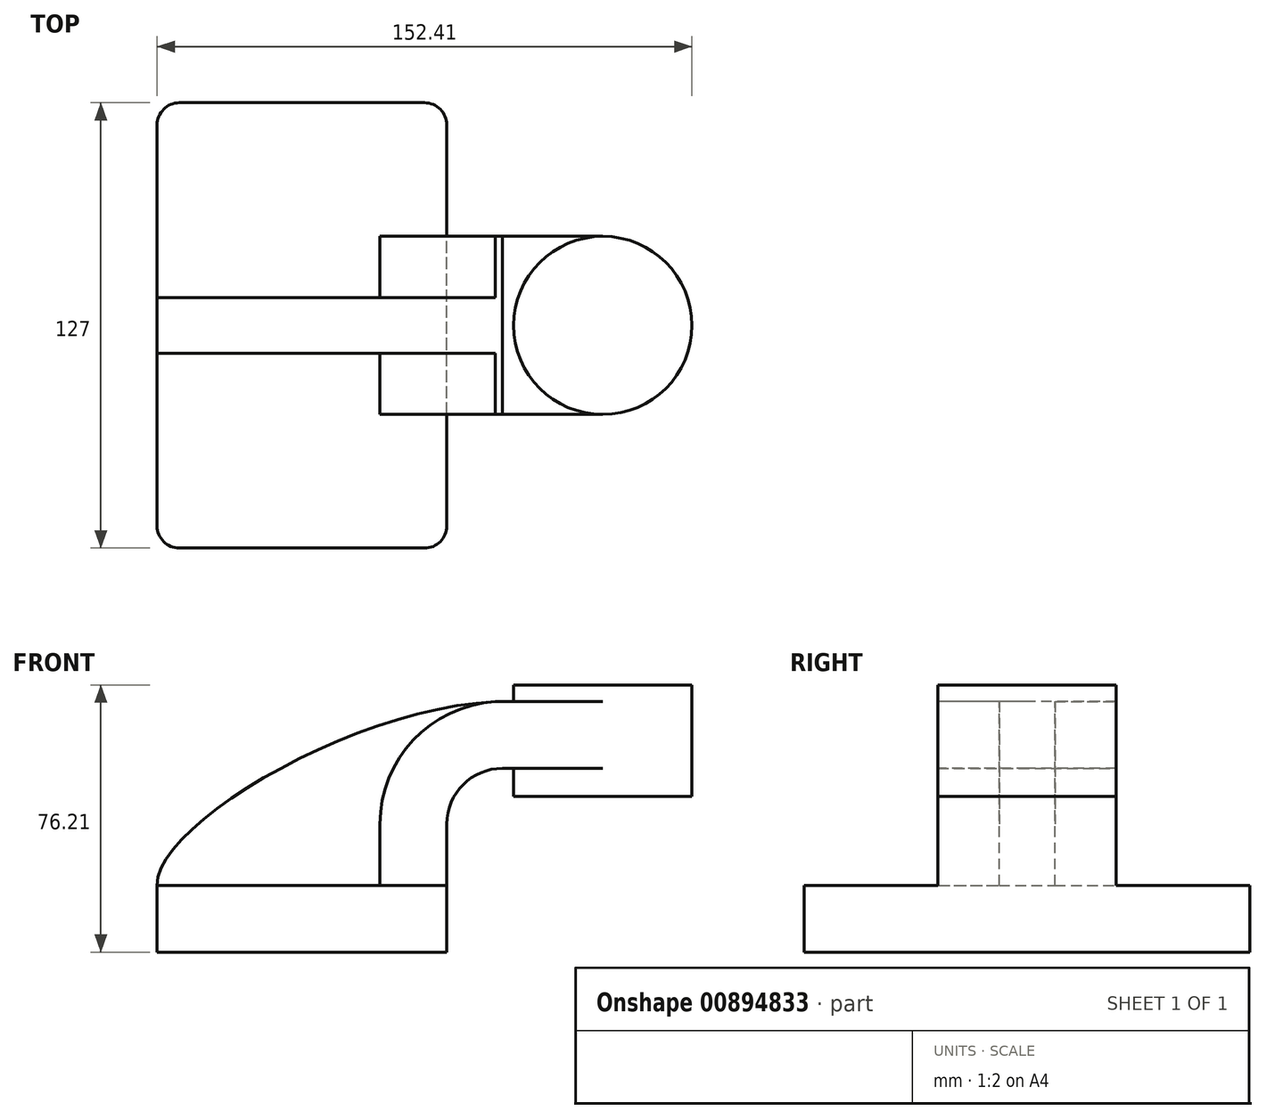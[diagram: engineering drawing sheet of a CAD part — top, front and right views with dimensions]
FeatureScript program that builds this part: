
annotation { "Feature Type Name" : "Feature", "Feature Type Description" : "" }
export const myFeature = defineFeature(function(context is Context, id is Id, definition is map)
    precondition{}
    {
        {
            var Q0;
            Q0=qCreatedBy(makeId("Front.planeOp"),FACE);
            var sketch = newSketch(context, id + "F0", { "sketchPlane" : qUnion([Q0])});
            skLineSegment(sketch, "E0.bottom", {"start": v(-41.28, 9.52) * mm, "end": v(41.28, 9.53) * mm});
            skLineSegment(sketch, "E0.top", {"start": v(-41.28, -9.53) * mm, "end": v(41.28, -9.53) * mm});
            skLineSegment(sketch, "E0.left", {"start": v(-41.28, 9.52) * mm, "end": v(-41.28, -9.53) * mm});
            skLineSegment(sketch, "E0.right", {"start": v(41.28, 9.53) * mm, "end": v(41.28, -9.52) * mm});
            skPoint(sketch, "E0.middle", {"position": v(0, 0) * mm});
            skLineSegment(sketch, "E1.bottom", {"start": v(60.32, 66.67) * mm, "end": v(111.12, 66.67) * mm});
            skLineSegment(sketch, "E1.top", {"start": v(60.32, 34.92) * mm, "end": v(111.12, 34.92) * mm});
            skLineSegment(sketch, "E1.left", {"start": v(60.32, 66.67) * mm, "end": v(60.32, 34.92) * mm});
            skLineSegment(sketch, "E1.right", {"start": v(111.12, 66.67) * mm, "end": v(111.12, 34.92) * mm});
            skPoint(sketch, "E1.middle", {"position": v(85.72, 50.8) * mm});
            skLineSegment(sketch, "E2", {"start": v(41.28, 9.53) * mm, "end": v(41.28, 27) * mm});
            skArc(sketch, "E3", {"start": v(41.27, 27) * mm, "mid": v(45.92, 38.23) * mm, "end": v(57.15, 42.88) * mm});
            skLineSegment(sketch, "E4", {"start": v(57.15, 42.88) * mm, "end": v(85.72, 42.88) * mm});
            skLineSegment(sketch, "E5.0", {"start": v(57.15, 61.93) * mm, "end": v(85.72, 61.93) * mm});
            skArc(sketch, "E5.1", {"start": v(22.23, 27) * mm, "mid": v(32.45, 51.7) * mm, "end": v(57.15, 61.93) * mm});
            skLineSegment(sketch, "E5.2", {"start": v(22.22, 9.53) * mm, "end": v(22.22, 27) * mm});
            skLineSegment(sketch, "E6", {"start": v(85.72, 61.93) * mm, "end": v(85.72, 42.88) * mm});
            skFitSpline(sketch, "E7", {"points": [v(-41.28, 9.52) * mm, v(57.15, 61.93) * mm], "startDerivative": vector(-1.37, 53.03) * mm, "endDerivative": vector(121.67, 1.99) * mm});
            skLineSegment(sketch, "E8", {"start": v(85.72, 34.92) * mm, "end": v(85.72, 66.67) * mm});
            skSolve(sketch);
        }
        {
            var Q0;
            Q0=makeQuery(id+"F0.imprint","IMPRINT",FACE,{"disambiguationData":[TD([[makeQuery(id+"F0.imprint","IMPRINT",EDGE,{"derivedFrom":sQuery(id+"F0.wireOp",EDGE,"E0.top")}),1.0]])]});
            extrude(context, id + "F1", {"entities" : qUnion([Q0]), "endBound" : BoundingType.SYMMETRIC, "depth" : 127 * mm, "offsetDistance" : 25.4 * mm});
        }
        {
            var Q0;
            {var subQ1=sQuery(id+"F0.wireOp",EDGE,"E2");Q0=makeQuery(id+"F0.imprint","IMPRINT",FACE,{"disambiguationData":[TD([[makeQuery(id+"F0.imprint","IMPRINT",EDGE,{"derivedFrom":subQ1}),1.0]])]});}
            var Q1;
            {var subQ5=sQuery(id+"F0.wireOp",EDGE,"E6");Q1=makeQuery(id+"F0.imprint","IMPRINT",FACE,{"disambiguationData":[TD([[makeQuery(id+"F0.imprint","IMPRINT",EDGE,{"derivedFrom":subQ5}),-1.0]])]});}
            var Q2;
            {var subQ0=sQuery(id+"F0.wireOp",EDGE,"E5.0");var subQ1=sQuery(id+"F0.wireOp",EDGE,"E1.left");var subQ2=makeQuery(id+"F0.imprint","INTERSECT",VERTEX,{"derivedFrom":[subQ1,subQ0]});Q2=makeQuery(id+"F0.imprint","IMPRINT",FACE,{"disambiguationData":[TD([[makeQuery(id+"F0.imprint","IMPRINT",EDGE,{"disambiguationData":[TD([[subQ2,-1.0]])],"derivedFrom":subQ1}),1.0]])]});}
            extrude(context, id + "F2", {"entities" : qUnion([Q0, Q1, Q2]), "operationType" : NewBodyOperationType.ADD, "endBound" : BoundingType.SYMMETRIC, "depth" : 50.8 * mm, "offsetDistance" : 25.4 * mm});
        }
        {
            var Q0;
            {var subQ3=sQuery(id+"F0.wireOp",EDGE,"E5.2");Q0=makeQuery(id+"F0.imprint","IMPRINT",FACE,{"disambiguationData":[TD([[makeQuery(id+"F0.imprint","IMPRINT",EDGE,{"derivedFrom":subQ3}),1.0]])]});}
            extrude(context, id + "F3", {"entities" : qUnion([Q0]), "operationType" : NewBodyOperationType.ADD, "endBound" : BoundingType.SYMMETRIC, "depth" : 15.88 * mm, "offsetDistance" : 25.4 * mm});
        }
        {
            var Q0;
            {var subQ4=sQuery(id+"F0.wireOp",EDGE,"E1.right");Q0=makeQuery(id+"F0.imprint","IMPRINT",FACE,{"disambiguationData":[TD([[makeQuery(id+"F0.imprint","IMPRINT",EDGE,{"derivedFrom":subQ4}),-1.0]])]});}
            var Q1;
            Q1=sQuery(id+"F0.wireOp",EDGE,"E8");
            revolve(context, id + "F4", {"operationType" : NewBodyOperationType.ADD, "surfaceOperationType" : NewSurfaceOperationType.NEW, "entities" : qUnion([Q0]), "axis" : qUnion([Q1]), "revolveType" : RevolveType.FULL});
        }
        {
            var Q0;
            Q0=makeQuery(id+"F1.opExtrude","CAP_EDGE",EDGE,{"disambiguationData":[OSD([sQuery(id+"F0.wireOp",EDGE,"E0.left")])],"isStart":false});
            var Q1;
            Q1=makeQuery(id+"F1.opExtrude","CAP_EDGE",EDGE,{"disambiguationData":[OSD([sQuery(id+"F0.wireOp",EDGE,"E0.right")])],"isStart":false});
            var Q2;
            Q2=makeQuery(id+"F1.opExtrude","CAP_EDGE",EDGE,{"disambiguationData":[OSD([sQuery(id+"F0.wireOp",EDGE,"E0.right")])],"isStart":true});
            var Q3;
            Q3=makeQuery(id+"F1.opExtrude","CAP_EDGE",EDGE,{"disambiguationData":[OSD([sQuery(id+"F0.wireOp",EDGE,"E0.left")])],"isStart":true});
            fillet(context, id + "F5", {"entities" : qUnion([Q0, Q1, Q2, Q3]), "radius" : 6.35 * mm, "tangentPropagation" : true, "allowEdgeOverflow" : false});
        }
    });
